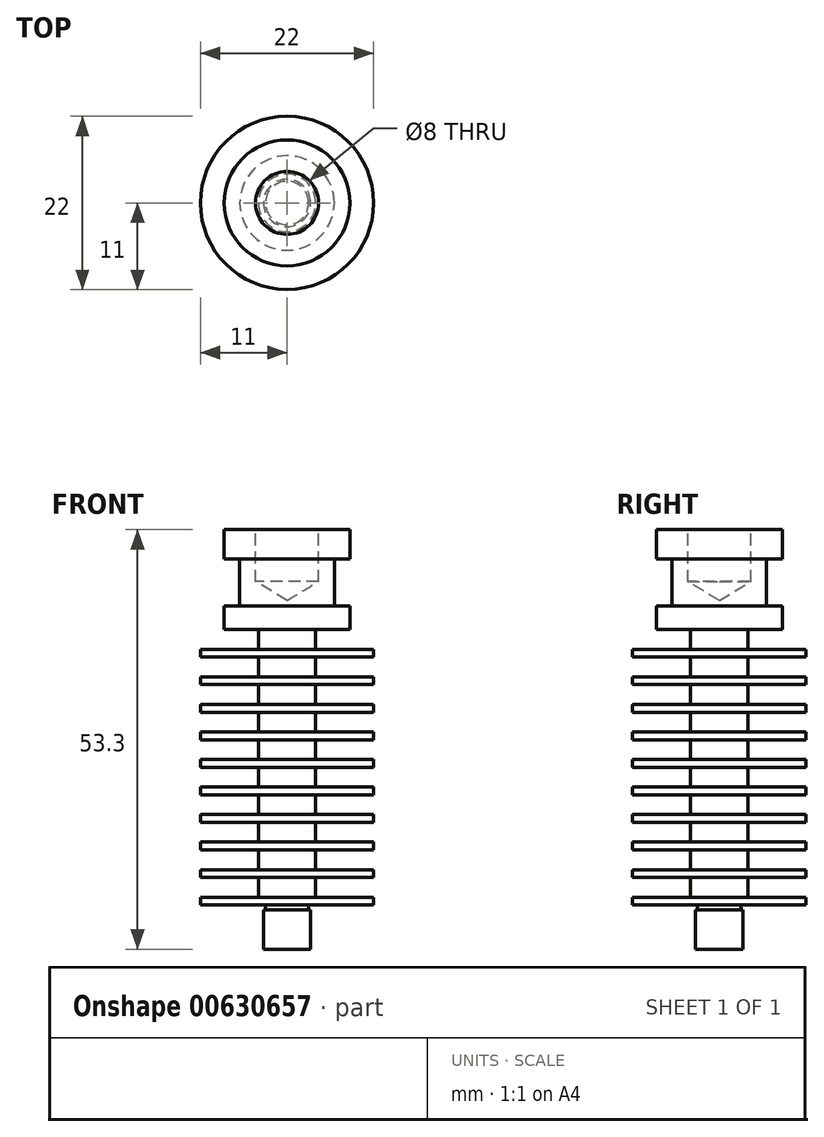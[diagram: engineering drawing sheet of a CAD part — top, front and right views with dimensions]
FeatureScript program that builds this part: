
annotation { "Feature Type Name" : "Feature", "Feature Type Description" : "" }
export const myFeature = defineFeature(function(context is Context, id is Id, definition is map)
    precondition{}
    {
        {
            var Q0;
            Q0=qCreatedBy(makeId("Front.planeOp"),FACE);
            var sketch = newSketch(context, id + "F0", { "sketchPlane" : qUnion([Q0])});
            skLineSegment(sketch, "E0", {"start": v(0, -10.1) * mm, "end": v(3, -10.1) * mm});
            skLineSegment(sketch, "E1", {"start": v(3, -10.1) * mm, "end": v(3, -5.1) * mm});
            skLineSegment(sketch, "E2", {"start": v(3, -5.1) * mm, "end": v(2.75, -5.1) * mm});
            skLineSegment(sketch, "E3", {"start": v(2.75, -5.1) * mm, "end": v(2.75, -4.5) * mm});
            skLineSegment(sketch, "E4", {"start": v(2.75, -4.5) * mm, "end": v(11, -4.5) * mm});
            skLineSegment(sketch, "E5", {"start": v(11, -4.5) * mm, "end": v(11, -3.5) * mm});
            skLineSegment(sketch, "E6", {"start": v(11, -3.5) * mm, "end": v(3.65, -3.5) * mm});
            skLineSegment(sketch, "E7", {"start": v(3.65, -3.5) * mm, "end": v(3.65, -1) * mm});
            skLineSegment(sketch, "E8", {"start": v(3.65, -1) * mm, "end": v(11, -1) * mm});
            skLineSegment(sketch, "E9", {"start": v(11, -1) * mm, "end": v(11, 0) * mm});
            skLineSegment(sketch, "E10", {"start": v(11, 0) * mm, "end": v(3.65, 0) * mm});
            skLineSegment(sketch, "E11", {"start": v(3.65, 0) * mm, "end": v(3.65, 2.5) * mm});
            skLineSegment(sketch, "E12", {"start": v(3.65, 2.5) * mm, "end": v(11, 2.5) * mm});
            skLineSegment(sketch, "E13", {"start": v(11, 2.5) * mm, "end": v(11, 3.5) * mm});
            skLineSegment(sketch, "E14", {"start": v(11, 3.5) * mm, "end": v(3.65, 3.5) * mm});
            skLineSegment(sketch, "E15", {"start": v(3.65, 3.5) * mm, "end": v(3.65, 6) * mm});
            skLineSegment(sketch, "E16", {"start": v(3.65, 6) * mm, "end": v(11, 6) * mm});
            skLineSegment(sketch, "E17", {"start": v(11, 6) * mm, "end": v(11, 7) * mm});
            skLineSegment(sketch, "E18", {"start": v(11, 7) * mm, "end": v(3.65, 7) * mm});
            skLineSegment(sketch, "E19", {"start": v(3.65, 7) * mm, "end": v(3.65, 9.5) * mm});
            skLineSegment(sketch, "E20", {"start": v(3.65, 9.5) * mm, "end": v(11, 9.5) * mm});
            skLineSegment(sketch, "E21", {"start": v(11, 9.5) * mm, "end": v(11, 10.5) * mm});
            skLineSegment(sketch, "E22", {"start": v(11, 10.5) * mm, "end": v(3.65, 10.5) * mm});
            skLineSegment(sketch, "E23", {"start": v(3.65, 10.5) * mm, "end": v(3.65, 13) * mm});
            skLineSegment(sketch, "E24", {"start": v(3.65, 13) * mm, "end": v(11, 13) * mm});
            skLineSegment(sketch, "E25", {"start": v(11, 13) * mm, "end": v(11, 14) * mm});
            skLineSegment(sketch, "E26", {"start": v(11, 14) * mm, "end": v(3.65, 14) * mm});
            skLineSegment(sketch, "E27", {"start": v(3.65, 14) * mm, "end": v(3.65, 16.5) * mm});
            skLineSegment(sketch, "E28", {"start": v(3.65, 16.5) * mm, "end": v(11, 16.5) * mm});
            skLineSegment(sketch, "E29", {"start": v(11, 16.5) * mm, "end": v(11, 17.5) * mm});
            skLineSegment(sketch, "E30", {"start": v(11, 17.5) * mm, "end": v(3.65, 17.5) * mm});
            skLineSegment(sketch, "E31", {"start": v(3.65, 17.5) * mm, "end": v(3.65, 20) * mm});
            skLineSegment(sketch, "E32", {"start": v(3.65, 20) * mm, "end": v(11, 20) * mm});
            skLineSegment(sketch, "E33", {"start": v(11, 20) * mm, "end": v(11, 21) * mm});
            skLineSegment(sketch, "E34", {"start": v(11, 21) * mm, "end": v(3.65, 21) * mm});
            skLineSegment(sketch, "E35", {"start": v(3.65, 21) * mm, "end": v(3.65, 23.5) * mm});
            skLineSegment(sketch, "E36", {"start": v(3.65, 23.5) * mm, "end": v(11, 23.5) * mm});
            skLineSegment(sketch, "E37", {"start": v(11, 23.5) * mm, "end": v(11, 24.5) * mm});
            skLineSegment(sketch, "E38", {"start": v(11, 24.5) * mm, "end": v(3.65, 24.5) * mm});
            skLineSegment(sketch, "E39", {"start": v(3.65, 24.5) * mm, "end": v(3.65, 27) * mm});
            skLineSegment(sketch, "E40", {"start": v(3.65, 27) * mm, "end": v(11, 27) * mm});
            skLineSegment(sketch, "E41", {"start": v(11, 27) * mm, "end": v(11, 28) * mm});
            skLineSegment(sketch, "E42", {"start": v(11, 28) * mm, "end": v(3.65, 28) * mm});
            skLineSegment(sketch, "E43", {"start": v(3.65, 28) * mm, "end": v(3.65, 30.5) * mm});
            skLineSegment(sketch, "E44", {"start": v(3.65, 30.5) * mm, "end": v(8, 30.5) * mm});
            skLineSegment(sketch, "E45", {"start": v(8, 30.5) * mm, "end": v(8, 33.5) * mm});
            skLineSegment(sketch, "E46", {"start": v(8, 33.5) * mm, "end": v(6, 33.5) * mm});
            skLineSegment(sketch, "E47", {"start": v(6, 33.5) * mm, "end": v(6, 39.5) * mm});
            skLineSegment(sketch, "E48", {"start": v(6, 39.5) * mm, "end": v(8, 39.5) * mm});
            skLineSegment(sketch, "E49", {"start": v(8, 39.5) * mm, "end": v(8, 43.2) * mm});
            skLineSegment(sketch, "E50", {"start": v(8, 43.2) * mm, "end": v(0, 43.2) * mm});
            skLineSegment(sketch, "E51", {"start": v(0, 43.2) * mm, "end": v(0, -10.1) * mm});
            skSolve(sketch);
        }
        {
            var Q0;
            Q0=makeQuery(id+"F0.imprint","IMPRINT",FACE,{"disambiguationData":[TD([[makeQuery(id+"F0.imprint","IMPRINT",EDGE,{"derivedFrom":sQuery(id+"F0.wireOp",EDGE,"E0")}),1.0]])]});
            var Q1;
            Q1=sQuery(id+"F0.wireOp",EDGE,"E51");
            revolve(context, id + "F1", {"entities" : qUnion([Q0]), "axis" : qUnion([Q1]), "revolveType" : RevolveType.FULL});
        }
        {
            var Q0;
            Q0=makeQuery(id+"F1.opRevolve","SWEPT_FACE",FACE,{"disambiguationData":[OSD([sQuery(id+"F0.wireOp",EDGE,"E50")])]});
            var sketch = newSketch(context, id + "F2", { "sketchPlane" : qUnion([Q0])});
            skCircle(sketch, "E52", {"center": v(0, 0) * mm, "radius": 4 * mm});
            skSolve(sketch);
        }
        {
            var Q0;
            Q0=sQuery(id+"F2.wireOp",VERTEX,"E52.center");
            var Q1;
            Q1=makeQuery(id+"F1.opRevolve","SWEPT_BODY",BODY,{"disambiguationData":[OSD([sQuery(id+"F0.wireOp",EDGE,"E0"),sQuery(id+"F0.wireOp",EDGE,"E1"),sQuery(id+"F0.wireOp",EDGE,"E2"),sQuery(id+"F0.wireOp",EDGE,"E3"),sQuery(id+"F0.wireOp",EDGE,"E4"),sQuery(id+"F0.wireOp",EDGE,"E5"),sQuery(id+"F0.wireOp",EDGE,"E6"),sQuery(id+"F0.wireOp",EDGE,"E7"),sQuery(id+"F0.wireOp",EDGE,"E8"),sQuery(id+"F0.wireOp",EDGE,"E9"),sQuery(id+"F0.wireOp",EDGE,"E10"),sQuery(id+"F0.wireOp",EDGE,"E11"),sQuery(id+"F0.wireOp",EDGE,"E12"),sQuery(id+"F0.wireOp",EDGE,"E13"),sQuery(id+"F0.wireOp",EDGE,"E14"),sQuery(id+"F0.wireOp",EDGE,"E15"),sQuery(id+"F0.wireOp",EDGE,"E16"),sQuery(id+"F0.wireOp",EDGE,"E17"),sQuery(id+"F0.wireOp",EDGE,"E18"),sQuery(id+"F0.wireOp",EDGE,"E19"),sQuery(id+"F0.wireOp",EDGE,"E20"),sQuery(id+"F0.wireOp",EDGE,"E21"),sQuery(id+"F0.wireOp",EDGE,"E22"),sQuery(id+"F0.wireOp",EDGE,"E23"),sQuery(id+"F0.wireOp",EDGE,"E24"),sQuery(id+"F0.wireOp",EDGE,"E25"),sQuery(id+"F0.wireOp",EDGE,"E26"),sQuery(id+"F0.wireOp",EDGE,"E27"),sQuery(id+"F0.wireOp",EDGE,"E28"),sQuery(id+"F0.wireOp",EDGE,"E29"),sQuery(id+"F0.wireOp",EDGE,"E30"),sQuery(id+"F0.wireOp",EDGE,"E31"),sQuery(id+"F0.wireOp",EDGE,"E32"),sQuery(id+"F0.wireOp",EDGE,"E33"),sQuery(id+"F0.wireOp",EDGE,"E34"),sQuery(id+"F0.wireOp",EDGE,"E35"),sQuery(id+"F0.wireOp",EDGE,"E36"),sQuery(id+"F0.wireOp",EDGE,"E37"),sQuery(id+"F0.wireOp",EDGE,"E38"),sQuery(id+"F0.wireOp",EDGE,"E39"),sQuery(id+"F0.wireOp",EDGE,"E40"),sQuery(id+"F0.wireOp",EDGE,"E41"),sQuery(id+"F0.wireOp",EDGE,"E42"),sQuery(id+"F0.wireOp",EDGE,"E43"),sQuery(id+"F0.wireOp",EDGE,"E44"),sQuery(id+"F0.wireOp",EDGE,"E45"),sQuery(id+"F0.wireOp",EDGE,"E46"),sQuery(id+"F0.wireOp",EDGE,"E47"),sQuery(id+"F0.wireOp",EDGE,"E48"),sQuery(id+"F0.wireOp",EDGE,"E49"),sQuery(id+"F0.wireOp",EDGE,"E50"),sQuery(id+"F0.wireOp",EDGE,"E51")])]});
            hole(context, id + "F3", {"style" : HoleStyle.SIMPLE, "endStyle" : HoleEndStyle.BLIND, "holeDiameter" : 8 * mm, "holeDepth" : 6.6 * mm, "isTappedThrough" : true, "tappedDepth" : 12 * mm, "tapClearance" : 3, "locations" : qUnion([Q0]), "scope" : qUnion([Q1])});
        }
    });
